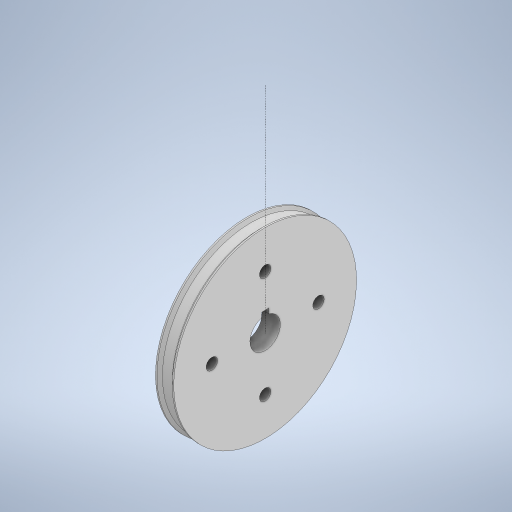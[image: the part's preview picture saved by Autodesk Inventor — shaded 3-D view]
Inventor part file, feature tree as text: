
AUTODESK INVENTOR PART (.ipt)
format: ipt  version: 2024 (Build 280153000, 153)  size: 288,256 bytes
history: native  units: mm
features: sketch x5, extrude x3, revolve x1
ambient origin geometry x8: Origin, YZ Plane, XZ Plane, XY Plane, X Axis, Y Axis, Z Axis, Center Point
bodies: Solid1 (feature_tree)
feature tree (9):
  sketch  "Sketch1"  dims[d0=120.0mm d1=600.0mm]
  sketch  "Sketch2"  dims[d3=10.0mm d4=10.0mm]
  sketch  "Sketch3"  dims[d5=32.32mm d6=32.32mm]
  revolve  "Revolution1"  [1 undecoded]
  extrude  "Extrusion1"  Depth=10.0mm
  extrude  "Extrusion2"  Depth=32.32mm
  extrude  "Extrusion3"  TaperAngle=90.0deg  [1 undecoded]
  sketch  "Sketch4"  dims[d7=200.0mm d8=90.0deg]
  sketch  "Sketch5"  dims[d9=0.0mm d10=0.0mm d11=25.0mm d12=130.0mm d13=0.0mm d14=0.0mm d15=350.0mm d16=350.0mm d17=350.0mm d18=350.0mm d19=75.0mm d20=75.0mm d21=75.0mm d22=75.0mm d23=0.0mm d24=0.0mm]
note: 2 required parameter values undecoded (feature->parameter linkage not recoverable at this tier; creation-order binding heuristic only, values carry confidence <= 0.55)